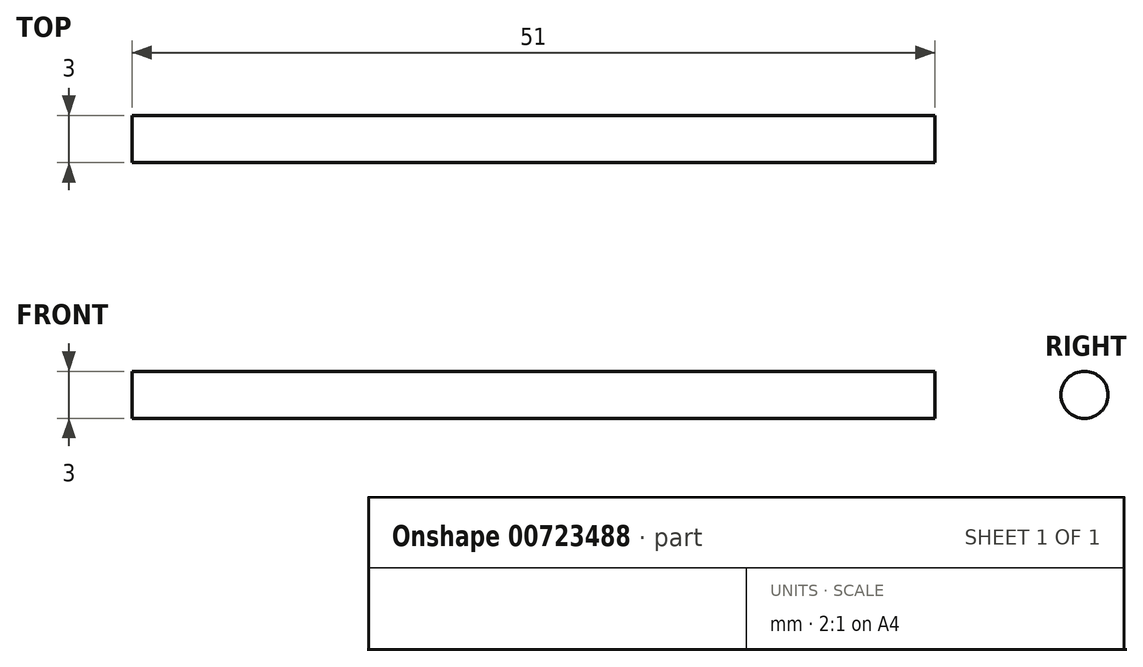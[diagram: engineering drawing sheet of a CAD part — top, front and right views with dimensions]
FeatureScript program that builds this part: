
annotation { "Feature Type Name" : "Feature", "Feature Type Description" : "" }
export const myFeature = defineFeature(function(context is Context, id is Id, definition is map)
    precondition{}
    {
        {
            var Q0;
            Q0=qCreatedBy(makeId("Right.planeOp"),FACE);
            var sketch = newSketch(context, id + "F0", { "sketchPlane" : qUnion([Q0])});
            skCircle(sketch, "E0", {"center": v(0, 0) * mm, "radius": 1.5 * mm});
            skSolve(sketch);
        }
        {
            var Q0;
            Q0 = qSketchRegion(id + "F0", true);
            extrude(context, id + "F1", {"entities" : qUnion([Q0]), "depth" : 51 * mm, "offsetDistance" : 25 * mm});
        }
    });
